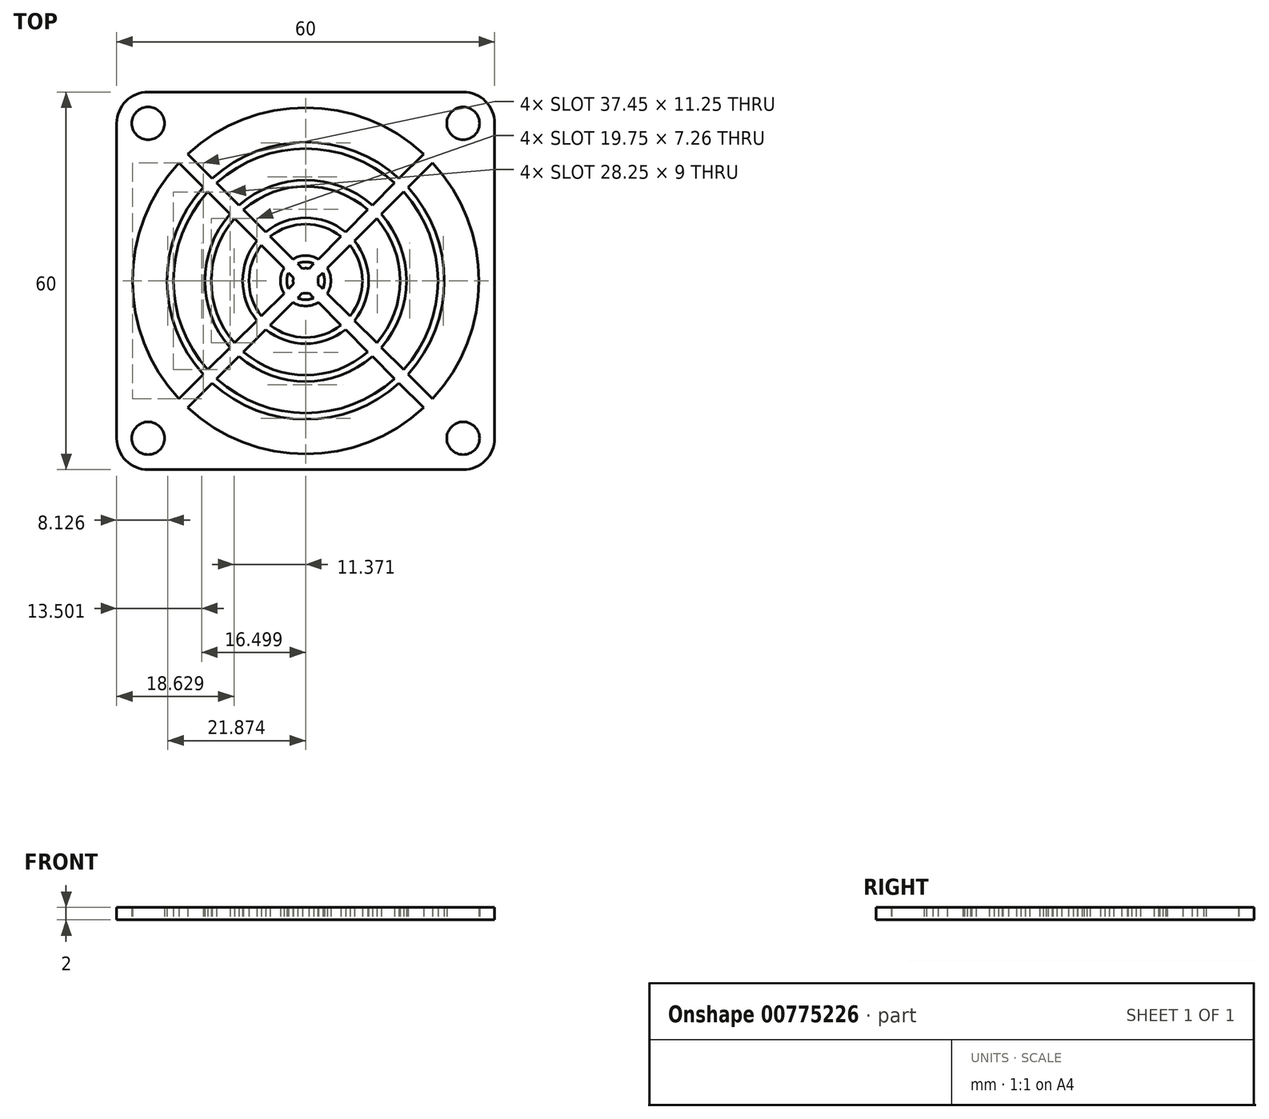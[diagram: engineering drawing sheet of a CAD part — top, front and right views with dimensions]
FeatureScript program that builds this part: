
annotation { "Feature Type Name" : "Feature", "Feature Type Description" : "" }
export const myFeature = defineFeature(function(context is Context, id is Id, definition is map)
    precondition{}
    {
        {
            var Q0;
            Q0=qCreatedBy(makeId("Top.planeOp"),FACE);
            var sketch = newSketch(context, id + "F0", { "sketchPlane" : qUnion([Q0])});
            skLineSegment(sketch, "E0.bottom", {"start": v(30, -30) * mm, "end": v(-30, -30) * mm});
            skLineSegment(sketch, "E0.top", {"start": v(30, 30) * mm, "end": v(-30, 30) * mm});
            skLineSegment(sketch, "E0.left", {"start": v(30, -30) * mm, "end": v(30, 30) * mm});
            skLineSegment(sketch, "E0.right", {"start": v(-30, -30) * mm, "end": v(-30, 30) * mm});
            skPoint(sketch, "E0.middle", {"position": v(0, 0) * mm});
            skCircle(sketch, "E1", {"center": v(-25, 25) * mm, "radius": 2.6 * mm});
            skCircle(sketch, "E2.MirrorC", {"center": v(25, 25) * mm, "radius": 2.6 * mm});
            skCircle(sketch, "E3.MirrorC", {"center": v(25, -25) * mm, "radius": 2.6 * mm});
            skCircle(sketch, "E4.MirrorC", {"center": v(-25, -25) * mm, "radius": 2.6 * mm});
            skArc(sketch, "E5", {"start": v(-2.7, 1.3) * mm, "mid": v(-3, 0) * mm, "end": v(-2.7, -1.3) * mm});
            skArc(sketch, "E6", {"start": v(-2.03, -3.45) * mm, "mid": v(0, -4) * mm, "end": v(2.03, -3.45) * mm});
            skArc(sketch, "E7", {"start": v(-12, 10.58) * mm, "mid": v(-16, 0) * mm, "end": v(-12, -10.58) * mm});
            skArc(sketch, "E8", {"start": v(-15.54, 14.13) * mm, "mid": v(-21, 0) * mm, "end": v(-15.54, -14.13) * mm});
            skArc(sketch, "E9", {"start": v(-16.25, 14.83) * mm, "mid": v(-22, 0) * mm, "end": v(-16.25, -14.83) * mm});
            skArc(sketch, "E10", {"start": v(-20.14, 18.73) * mm, "mid": v(-27.5, 0) * mm, "end": v(-20.14, -18.73) * mm});
            skLineSegment(sketch, "E11", {"start": v(0, 0) * mm, "end": v(-25, 25) * mm, "construction": true});
            skLineSegment(sketch, "E12", {"start": v(0, 0) * mm, "end": v(25, 25) * mm, "construction": true});
            skLineSegment(sketch, "E13", {"start": v(25, -25) * mm, "end": v(0, 0) * mm, "construction": true});
            skLineSegment(sketch, "E14", {"start": v(-25, -25) * mm, "end": v(0, 0) * mm, "construction": true});
            skArc(sketch, "E15", {"start": v(1.93, -0.52) * mm, "mid": v(2, 0) * mm, "end": v(1.93, 0.52) * mm});
            skLineSegment(sketch, "E16", {"start": v(-20.14, 18.73) * mm, "end": v(-16.25, 14.83) * mm});
            skLineSegment(sketch, "E17.MirrorCS", {"start": v(-18.73, 20.14) * mm, "end": v(-14.83, 16.25) * mm});
            skLineSegment(sketch, "E18.MirrorCS", {"start": v(-20.14, -18.73) * mm, "end": v(-16.25, -14.83) * mm});
            skLineSegment(sketch, "E19.MirrorCS", {"start": v(-18.73, -20.14) * mm, "end": v(-14.83, -16.25) * mm});
            skLineSegment(sketch, "E20.MirrorCS", {"start": v(18.73, 20.14) * mm, "end": v(14.83, 16.25) * mm});
            skLineSegment(sketch, "E21.MirrorCS", {"start": v(20.14, 18.73) * mm, "end": v(16.25, 14.83) * mm});
            skLineSegment(sketch, "E22.MirrorCS", {"start": v(20.14, -18.73) * mm, "end": v(16.25, -14.83) * mm});
            skLineSegment(sketch, "E23.MirrorCS", {"start": v(18.73, -20.14) * mm, "end": v(14.83, -16.25) * mm});
            skArc(sketch, "E24.trimOffspring", {"start": v(-1.93, 0.52) * mm, "mid": v(-2, 0) * mm, "end": v(-1.93, -0.52) * mm});
            skArc(sketch, "E25.trimOffspring", {"start": v(-0.52, -1.93) * mm, "mid": v(0, -2) * mm, "end": v(0.52, -1.93) * mm});
            skArc(sketch, "E26.trimOffspring", {"start": v(-1.3, -2.7) * mm, "mid": v(0, -3) * mm, "end": v(1.3, -2.7) * mm});
            skArc(sketch, "E27.trimOffspring", {"start": v(-18.73, -20.14) * mm, "mid": v(0, -27.5) * mm, "end": v(18.73, -20.14) * mm});
            skArc(sketch, "E28.trimOffspring", {"start": v(-14.83, -16.25) * mm, "mid": v(0, -22) * mm, "end": v(14.83, -16.25) * mm});
            skArc(sketch, "E29.trimOffspring", {"start": v(-14.13, -15.54) * mm, "mid": v(0, -21) * mm, "end": v(14.13, -15.54) * mm});
            skArc(sketch, "E30.trimOffspring", {"start": v(-10.58, -12) * mm, "mid": v(0, -16) * mm, "end": v(10.58, -12) * mm});
            skArc(sketch, "E31.trimOffspring", {"start": v(12, -10.58) * mm, "mid": v(16, 0) * mm, "end": v(12, 10.58) * mm});
            skArc(sketch, "E32", {"start": v(-11.3, 9.88) * mm, "mid": v(-15, 0) * mm, "end": v(-11.3, -9.88) * mm});
            skArc(sketch, "E33", {"start": v(-7.03, 5.62) * mm, "mid": v(-9, 0) * mm, "end": v(-7.03, -5.62) * mm});
            skArc(sketch, "E34", {"start": v(-7.74, 6.33) * mm, "mid": v(-10, 0) * mm, "end": v(-7.74, -6.33) * mm});
            skLineSegment(sketch, "E35.trimOffspring", {"start": v(-15.54, 14.13) * mm, "end": v(-12, 10.58) * mm});
            skLineSegment(sketch, "E36.trimOffspring", {"start": v(-14.13, 15.54) * mm, "end": v(-10.58, 12) * mm});
            skLineSegment(sketch, "E37.trimOffspring", {"start": v(-11.3, 9.88) * mm, "end": v(-7.74, 6.33) * mm});
            skLineSegment(sketch, "E38.trimOffspring", {"start": v(-9.88, 11.3) * mm, "end": v(-6.33, 7.74) * mm});
            skLineSegment(sketch, "E39.trimOffspring", {"start": v(-5.62, 7.03) * mm, "end": v(-2.03, 3.45) * mm});
            skLineSegment(sketch, "E40.trimOffspring", {"start": v(-7.03, 5.62) * mm, "end": v(-3.45, 2.03) * mm});
            skArc(sketch, "E41.trimOffspring", {"start": v(-6.33, -7.74) * mm, "mid": v(0, -10) * mm, "end": v(6.33, -7.74) * mm});
            skArc(sketch, "E42.trimOffspring", {"start": v(-5.62, -7.03) * mm, "mid": v(0, -9) * mm, "end": v(5.62, -7.03) * mm});
            skArc(sketch, "E43.trimOffspring", {"start": v(-9.88, -11.3) * mm, "mid": v(0, -15) * mm, "end": v(9.88, -11.3) * mm});
            skLineSegment(sketch, "E44.trimOffspring", {"start": v(-9.88, -11.3) * mm, "end": v(-6.33, -7.74) * mm});
            skLineSegment(sketch, "E45.trimOffspring", {"start": v(-11.3, -9.88) * mm, "end": v(-7.74, -6.33) * mm});
            skLineSegment(sketch, "E46.trimOffspring", {"start": v(-7.03, -5.62) * mm, "end": v(-3.45, -2.03) * mm});
            skLineSegment(sketch, "E47.trimOffspring", {"start": v(-5.62, -7.03) * mm, "end": v(-2.03, -3.45) * mm});
            skArc(sketch, "E48.trimOffspring", {"start": v(-3.45, 2.03) * mm, "mid": v(-4, 0) * mm, "end": v(-3.45, -2.03) * mm});
            skLineSegment(sketch, "E49.trimOffspring", {"start": v(-1.3, 2.7) * mm, "end": v(-0.52, 1.93) * mm});
            skLineSegment(sketch, "E50.trimOffspring", {"start": v(-2.7, 1.3) * mm, "end": v(-1.93, 0.52) * mm});
            skLineSegment(sketch, "E51.trimOffspring", {"start": v(-2.7, -1.3) * mm, "end": v(-1.93, -0.52) * mm});
            skLineSegment(sketch, "E52.trimOffspring", {"start": v(-1.3, -2.7) * mm, "end": v(-0.52, -1.93) * mm});
            skLineSegment(sketch, "E53.trimOffspring", {"start": v(1.3, 2.7) * mm, "end": v(0.52, 1.93) * mm});
            skLineSegment(sketch, "E54.trimOffspring", {"start": v(2.7, 1.3) * mm, "end": v(1.93, 0.52) * mm});
            skArc(sketch, "E55.trimOffspring", {"start": v(2.03, 3.45) * mm, "mid": v(0, 4) * mm, "end": v(-2.03, 3.45) * mm});
            skArc(sketch, "E56.trimOffspring", {"start": v(1.3, 2.7) * mm, "mid": v(0, 3) * mm, "end": v(-1.3, 2.7) * mm});
            skArc(sketch, "E57.trimOffspring", {"start": v(0.52, 1.93) * mm, "mid": v(0, 2) * mm, "end": v(-0.52, 1.93) * mm});
            skArc(sketch, "E58.trimOffspring", {"start": v(11.3, -9.88) * mm, "mid": v(15, 0) * mm, "end": v(11.3, 9.88) * mm});
            skArc(sketch, "E59.trimOffspring", {"start": v(15.54, -14.13) * mm, "mid": v(21, 0) * mm, "end": v(15.54, 14.13) * mm});
            skArc(sketch, "E60.trimOffspring", {"start": v(16.25, -14.83) * mm, "mid": v(22, 0) * mm, "end": v(16.25, 14.83) * mm});
            skArc(sketch, "E61.trimOffspring", {"start": v(20.14, -18.73) * mm, "mid": v(27.5, 0) * mm, "end": v(20.14, 18.73) * mm});
            skArc(sketch, "E62.trimOffspring", {"start": v(18.73, 20.14) * mm, "mid": v(0, 27.5) * mm, "end": v(-18.73, 20.14) * mm});
            skPoint(sketch, "E63.orphan", {"position": v(24.01, 22.6) * mm});
            skPoint(sketch, "E64.orphan", {"position": v(22.6, 24.01) * mm});
            skPoint(sketch, "E65.orphan", {"position": v(24.01, -22.6) * mm});
            skPoint(sketch, "E66.orphan", {"position": v(22.6, -24.01) * mm});
            skPoint(sketch, "E67.orphan", {"position": v(-22.6, -24.01) * mm});
            skPoint(sketch, "E68.orphan", {"position": v(-24.01, -22.6) * mm});
            skPoint(sketch, "E69.orphan", {"position": v(-22.6, 24.01) * mm});
            skPoint(sketch, "E70.orphan", {"position": v(-24.01, 22.6) * mm});
            skArc(sketch, "E71.trimOffspring", {"start": v(14.83, 16.25) * mm, "mid": v(0, 22) * mm, "end": v(-14.83, 16.25) * mm});
            skArc(sketch, "E72.trimOffspring", {"start": v(14.13, 15.54) * mm, "mid": v(0, 21) * mm, "end": v(-14.13, 15.54) * mm});
            skLineSegment(sketch, "E73.trimOffspring", {"start": v(14.13, 15.54) * mm, "end": v(10.58, 12) * mm});
            skLineSegment(sketch, "E74.trimOffspring", {"start": v(15.54, 14.13) * mm, "end": v(12, 10.58) * mm});
            skLineSegment(sketch, "E75.trimOffspring", {"start": v(9.88, 11.3) * mm, "end": v(6.33, 7.74) * mm});
            skLineSegment(sketch, "E76.trimOffspring", {"start": v(11.3, 9.88) * mm, "end": v(7.74, 6.33) * mm});
            skArc(sketch, "E77.trimOffspring", {"start": v(10.58, 12) * mm, "mid": v(0, 16) * mm, "end": v(-10.58, 12) * mm});
            skArc(sketch, "E78.trimOffspring", {"start": v(9.88, 11.3) * mm, "mid": v(0, 15) * mm, "end": v(-9.88, 11.3) * mm});
            skArc(sketch, "E79.trimOffspring", {"start": v(5.62, 7.03) * mm, "mid": v(0, 9) * mm, "end": v(-5.62, 7.03) * mm});
            skArc(sketch, "E80.trimOffspring", {"start": v(6.33, 7.74) * mm, "mid": v(0, 10) * mm, "end": v(-6.33, 7.74) * mm});
            skLineSegment(sketch, "E81.trimOffspring", {"start": v(5.62, 7.03) * mm, "end": v(2.03, 3.45) * mm});
            skLineSegment(sketch, "E82.trimOffspring", {"start": v(7.03, 5.62) * mm, "end": v(3.45, 2.03) * mm});
            skLineSegment(sketch, "E83.trimOffspring", {"start": v(5.62, -7.03) * mm, "end": v(0.52, -1.93) * mm});
            skLineSegment(sketch, "E84.trimOffspring", {"start": v(7.03, -5.62) * mm, "end": v(1.93, -0.52) * mm});
            skArc(sketch, "E85.trimOffspring", {"start": v(7.03, -5.62) * mm, "mid": v(9, 0) * mm, "end": v(7.03, 5.62) * mm});
            skArc(sketch, "E86.trimOffspring", {"start": v(7.74, -6.33) * mm, "mid": v(10, 0) * mm, "end": v(7.74, 6.33) * mm});
            skArc(sketch, "E87.trimOffspring", {"start": v(3.45, -2.03) * mm, "mid": v(4, 0) * mm, "end": v(3.45, 2.03) * mm});
            skArc(sketch, "E88.trimOffspring", {"start": v(2.7, -1.3) * mm, "mid": v(3, 0) * mm, "end": v(2.7, 1.3) * mm});
            skLineSegment(sketch, "E89.trimOffspring", {"start": v(11.3, -9.88) * mm, "end": v(7.74, -6.33) * mm});
            skLineSegment(sketch, "E90.trimOffspring", {"start": v(9.88, -11.3) * mm, "end": v(6.33, -7.74) * mm});
            skLineSegment(sketch, "E91.trimOffspring", {"start": v(14.13, -15.54) * mm, "end": v(10.58, -12) * mm});
            skLineSegment(sketch, "E92.trimOffspring", {"start": v(15.54, -14.13) * mm, "end": v(12, -10.58) * mm});
            skLineSegment(sketch, "E93.trimOffspring", {"start": v(-15.54, -14.13) * mm, "end": v(-12, -10.58) * mm});
            skLineSegment(sketch, "E94.trimOffspring", {"start": v(-14.13, -15.54) * mm, "end": v(-10.58, -12) * mm});
            skSolve(sketch);
        }
        {
            var Q0;
            Q0 = qSketchRegion(id + "F0", true);
            extrude(context, id + "F1", {"entities" : qUnion([Q0]), "depth" : 2 * mm, "offsetDistance" : 25 * mm});
        }
        {
            var Q0;
            Q0=makeQuery(id+"F1.opExtrude","SWEPT_EDGE",EDGE,{"disambiguationData":[OSD([sQuery(id+"F0.wireOp",EDGE,"E0.top"),sQuery(id+"F0.wireOp",EDGE,"E0.left")])]});
            var Q1;
            Q1=makeQuery(id+"F1.opExtrude","SWEPT_EDGE",EDGE,{"disambiguationData":[OSD([sQuery(id+"F0.wireOp",EDGE,"E0.top"),sQuery(id+"F0.wireOp",EDGE,"E0.right")])]});
            var Q2;
            Q2=makeQuery(id+"F1.opExtrude","SWEPT_EDGE",EDGE,{"disambiguationData":[OSD([sQuery(id+"F0.wireOp",EDGE,"E0.bottom"),sQuery(id+"F0.wireOp",EDGE,"E0.right")])]});
            var Q3;
            Q3=makeQuery(id+"F1.opExtrude","SWEPT_EDGE",EDGE,{"disambiguationData":[OSD([sQuery(id+"F0.wireOp",EDGE,"E0.bottom"),sQuery(id+"F0.wireOp",EDGE,"E0.left")])]});
            fillet(context, id + "F2", {"entities" : qUnion([Q0, Q1, Q2, Q3]), "radius" : 5 * mm, "tangentPropagation" : true, "allowEdgeOverflow" : false});
        }
    });
